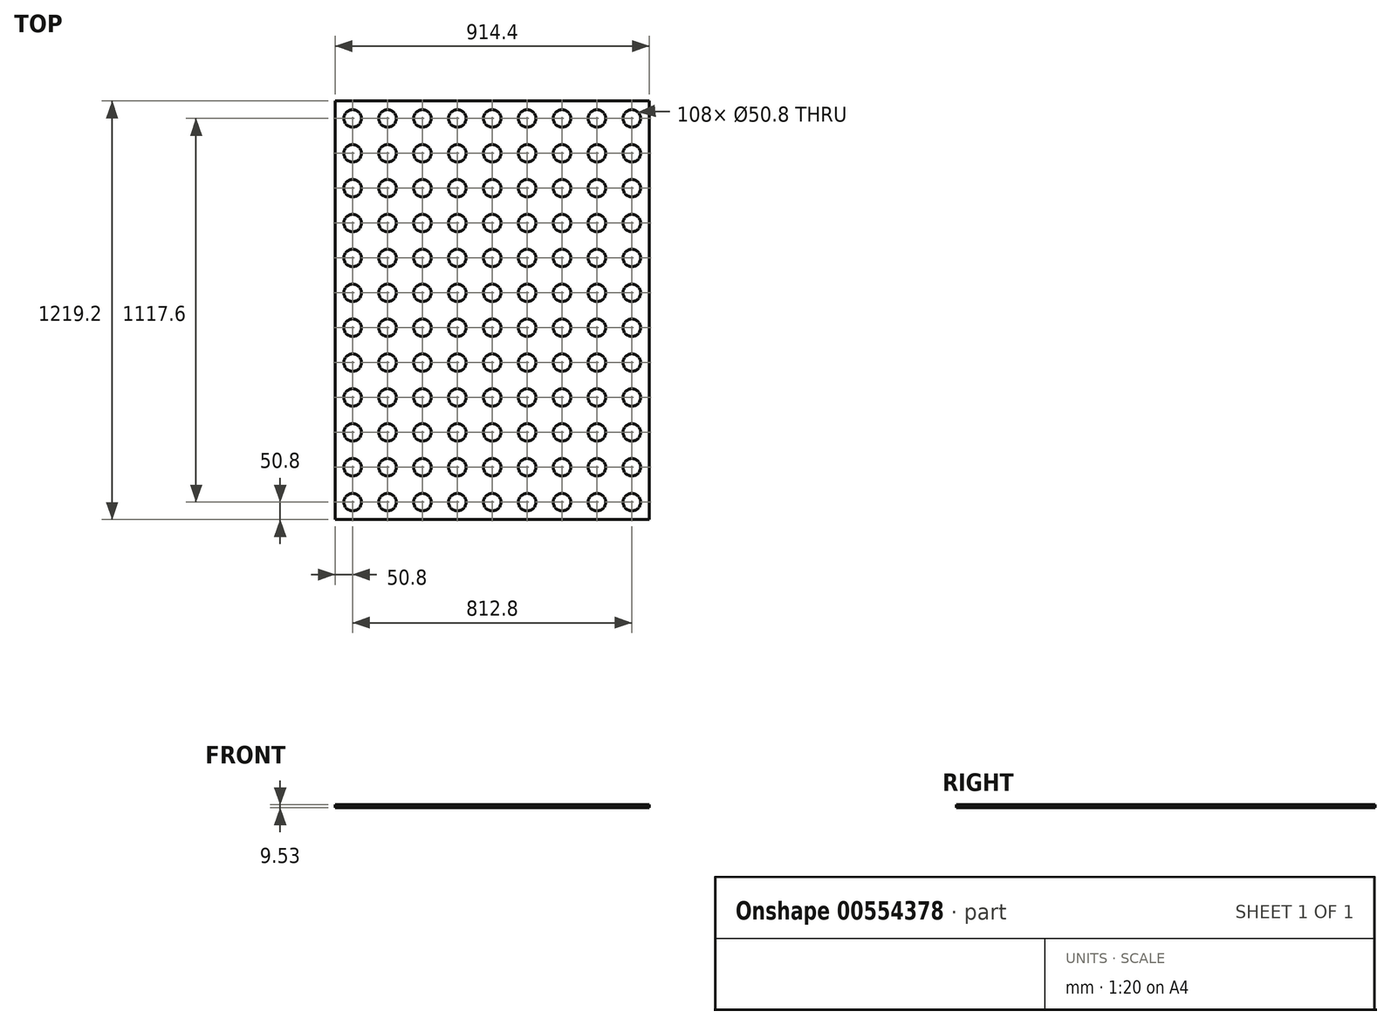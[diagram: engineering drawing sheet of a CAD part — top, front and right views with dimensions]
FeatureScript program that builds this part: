
annotation { "Feature Type Name" : "Feature", "Feature Type Description" : "" }
export const myFeature = defineFeature(function(context is Context, id is Id, definition is map)
    precondition{}
    {
        {
            var Q0;
            Q0=qCreatedBy(makeId("Top.planeOp"),FACE);
            var sketch = newSketch(context, id + "F0", { "sketchPlane" : qUnion([Q0])});
            skLineSegment(sketch, "E0.bottom", {"start": v(457.2, 609.6) * mm, "end": v(-457.2, 609.6) * mm});
            skLineSegment(sketch, "E0.top", {"start": v(457.2, -609.6) * mm, "end": v(-457.2, -609.6) * mm});
            skLineSegment(sketch, "E0.left", {"start": v(457.2, 609.6) * mm, "end": v(457.2, -609.6) * mm});
            skLineSegment(sketch, "E0.right", {"start": v(-457.2, 609.6) * mm, "end": v(-457.2, -609.6) * mm});
            skPoint(sketch, "E0.middle", {"position": v(0, 0) * mm});
            skSolve(sketch);
        }
        {
            var Q0;
            Q0 = qSketchRegion(id + "F0", true);
            extrude(context, id + "F1", {"entities" : qUnion([Q0]), "depth" : 9.52 * mm, "offsetDistance" : 25.4 * mm});
        }
        {
            var Q0;
            Q0=makeQuery(id+"F1.opExtrude","CAP_FACE",FACE,{"disambiguationData":[OSD([sQuery(id+"F0.wireOp",EDGE,"E0.bottom"),sQuery(id+"F0.wireOp",EDGE,"E0.top"),sQuery(id+"F0.wireOp",EDGE,"E0.left"),sQuery(id+"F0.wireOp",EDGE,"E0.right")])],"isStart":false});
            var sketch = newSketch(context, id + "F2", { "sketchPlane" : qUnion([Q0])});
            skCircle(sketch, "E1", {"center": v(-406.4, 558.8) * mm, "radius": 25.4 * mm});
            skCircle(sketch, "E2.1.0.0", {"center": v(-304.8, 558.8) * mm, "radius": 25.4 * mm});
            skCircle(sketch, "E2.2.0.0", {"center": v(-203.2, 558.8) * mm, "radius": 25.4 * mm});
            skCircle(sketch, "E2.3.0.0", {"center": v(-101.6, 558.8) * mm, "radius": 25.4 * mm});
            skCircle(sketch, "E2.4.0.0", {"center": v(0, 558.8) * mm, "radius": 25.4 * mm});
            skCircle(sketch, "E2.5.0.0", {"center": v(101.6, 558.8) * mm, "radius": 25.4 * mm});
            skCircle(sketch, "E2.6.0.0", {"center": v(203.2, 558.8) * mm, "radius": 25.4 * mm});
            skCircle(sketch, "E2.7.0.0", {"center": v(304.8, 558.8) * mm, "radius": 25.4 * mm});
            skCircle(sketch, "E2.8.0.0", {"center": v(406.4, 558.8) * mm, "radius": 25.4 * mm});
            skLineSegment(sketch, "E2.direction1", {"start": v(-406.4, 558.8) * mm, "end": v(-304.8, 558.8) * mm, "construction": true});
            skCircle(sketch, "E3.0.1.0", {"center": v(-101.6, 457.2) * mm, "radius": 25.4 * mm});
            skCircle(sketch, "E3.0.1.1", {"center": v(0, 457.2) * mm, "radius": 25.4 * mm});
            skCircle(sketch, "E3.0.1.2", {"center": v(101.6, 457.2) * mm, "radius": 25.4 * mm});
            skCircle(sketch, "E3.0.1.3", {"center": v(203.2, 457.2) * mm, "radius": 25.4 * mm});
            skLineSegment(sketch, "E3.0.1.4", {"start": v(-406.4, 457.2) * mm, "end": v(-304.8, 457.2) * mm, "construction": true});
            skCircle(sketch, "E3.0.1.5", {"center": v(406.4, 457.2) * mm, "radius": 25.4 * mm});
            skCircle(sketch, "E3.0.1.6", {"center": v(-203.2, 457.2) * mm, "radius": 25.4 * mm});
            skCircle(sketch, "E3.0.1.7", {"center": v(-304.8, 457.2) * mm, "radius": 25.4 * mm});
            skCircle(sketch, "E3.0.1.8", {"center": v(-406.4, 457.2) * mm, "radius": 25.4 * mm});
            skCircle(sketch, "E3.0.1.9", {"center": v(304.8, 457.2) * mm, "radius": 25.4 * mm});
            skCircle(sketch, "E3.0.2.0", {"center": v(-101.6, 355.6) * mm, "radius": 25.4 * mm});
            skCircle(sketch, "E3.0.2.1", {"center": v(0, 355.6) * mm, "radius": 25.4 * mm});
            skCircle(sketch, "E3.0.2.2", {"center": v(101.6, 355.6) * mm, "radius": 25.4 * mm});
            skCircle(sketch, "E3.0.2.3", {"center": v(203.2, 355.6) * mm, "radius": 25.4 * mm});
            skLineSegment(sketch, "E3.0.2.4", {"start": v(-406.4, 355.6) * mm, "end": v(-304.8, 355.6) * mm, "construction": true});
            skCircle(sketch, "E3.0.2.5", {"center": v(406.4, 355.6) * mm, "radius": 25.4 * mm});
            skCircle(sketch, "E3.0.2.6", {"center": v(-203.2, 355.6) * mm, "radius": 25.4 * mm});
            skCircle(sketch, "E3.0.2.7", {"center": v(-304.8, 355.6) * mm, "radius": 25.4 * mm});
            skCircle(sketch, "E3.0.2.8", {"center": v(-406.4, 355.6) * mm, "radius": 25.4 * mm});
            skCircle(sketch, "E3.0.2.9", {"center": v(304.8, 355.6) * mm, "radius": 25.4 * mm});
            skCircle(sketch, "E3.0.3.0", {"center": v(-101.6, 254) * mm, "radius": 25.4 * mm});
            skCircle(sketch, "E3.0.3.1", {"center": v(0, 254) * mm, "radius": 25.4 * mm});
            skCircle(sketch, "E3.0.3.2", {"center": v(101.6, 254) * mm, "radius": 25.4 * mm});
            skCircle(sketch, "E3.0.3.3", {"center": v(203.2, 254) * mm, "radius": 25.4 * mm});
            skLineSegment(sketch, "E3.0.3.4", {"start": v(-406.4, 254) * mm, "end": v(-304.8, 254) * mm, "construction": true});
            skCircle(sketch, "E3.0.3.5", {"center": v(406.4, 254) * mm, "radius": 25.4 * mm});
            skCircle(sketch, "E3.0.3.6", {"center": v(-203.2, 254) * mm, "radius": 25.4 * mm});
            skCircle(sketch, "E3.0.3.7", {"center": v(-304.8, 254) * mm, "radius": 25.4 * mm});
            skCircle(sketch, "E3.0.3.8", {"center": v(-406.4, 254) * mm, "radius": 25.4 * mm});
            skCircle(sketch, "E3.0.3.9", {"center": v(304.8, 254) * mm, "radius": 25.4 * mm});
            skCircle(sketch, "E3.0.4.0", {"center": v(-101.6, 152.4) * mm, "radius": 25.4 * mm});
            skCircle(sketch, "E3.0.4.1", {"center": v(0, 152.4) * mm, "radius": 25.4 * mm});
            skCircle(sketch, "E3.0.4.2", {"center": v(101.6, 152.4) * mm, "radius": 25.4 * mm});
            skCircle(sketch, "E3.0.4.3", {"center": v(203.2, 152.4) * mm, "radius": 25.4 * mm});
            skLineSegment(sketch, "E3.0.4.4", {"start": v(-406.4, 152.4) * mm, "end": v(-304.8, 152.4) * mm, "construction": true});
            skCircle(sketch, "E3.0.4.5", {"center": v(406.4, 152.4) * mm, "radius": 25.4 * mm});
            skCircle(sketch, "E3.0.4.6", {"center": v(-203.2, 152.4) * mm, "radius": 25.4 * mm});
            skCircle(sketch, "E3.0.4.7", {"center": v(-304.8, 152.4) * mm, "radius": 25.4 * mm});
            skCircle(sketch, "E3.0.4.8", {"center": v(-406.4, 152.4) * mm, "radius": 25.4 * mm});
            skCircle(sketch, "E3.0.4.9", {"center": v(304.8, 152.4) * mm, "radius": 25.4 * mm});
            skCircle(sketch, "E3.0.5.0", {"center": v(-101.6, 50.8) * mm, "radius": 25.4 * mm});
            skCircle(sketch, "E3.0.5.1", {"center": v(0, 50.8) * mm, "radius": 25.4 * mm});
            skCircle(sketch, "E3.0.5.2", {"center": v(101.6, 50.8) * mm, "radius": 25.4 * mm});
            skCircle(sketch, "E3.0.5.3", {"center": v(203.2, 50.8) * mm, "radius": 25.4 * mm});
            skLineSegment(sketch, "E3.0.5.4", {"start": v(-406.4, 50.8) * mm, "end": v(-304.8, 50.8) * mm, "construction": true});
            skCircle(sketch, "E3.0.5.5", {"center": v(406.4, 50.8) * mm, "radius": 25.4 * mm});
            skCircle(sketch, "E3.0.5.6", {"center": v(-203.2, 50.8) * mm, "radius": 25.4 * mm});
            skCircle(sketch, "E3.0.5.7", {"center": v(-304.8, 50.8) * mm, "radius": 25.4 * mm});
            skCircle(sketch, "E3.0.5.8", {"center": v(-406.4, 50.8) * mm, "radius": 25.4 * mm});
            skCircle(sketch, "E3.0.5.9", {"center": v(304.8, 50.8) * mm, "radius": 25.4 * mm});
            skCircle(sketch, "E3.0.6.0", {"center": v(-101.6, -50.8) * mm, "radius": 25.4 * mm});
            skCircle(sketch, "E3.0.6.1", {"center": v(0, -50.8) * mm, "radius": 25.4 * mm});
            skCircle(sketch, "E3.0.6.2", {"center": v(101.6, -50.8) * mm, "radius": 25.4 * mm});
            skCircle(sketch, "E3.0.6.3", {"center": v(203.2, -50.8) * mm, "radius": 25.4 * mm});
            skLineSegment(sketch, "E3.0.6.4", {"start": v(-406.4, -50.8) * mm, "end": v(-304.8, -50.8) * mm, "construction": true});
            skCircle(sketch, "E3.0.6.5", {"center": v(406.4, -50.8) * mm, "radius": 25.4 * mm});
            skCircle(sketch, "E3.0.6.6", {"center": v(-203.2, -50.8) * mm, "radius": 25.4 * mm});
            skCircle(sketch, "E3.0.6.7", {"center": v(-304.8, -50.8) * mm, "radius": 25.4 * mm});
            skCircle(sketch, "E3.0.6.8", {"center": v(-406.4, -50.8) * mm, "radius": 25.4 * mm});
            skCircle(sketch, "E3.0.6.9", {"center": v(304.8, -50.8) * mm, "radius": 25.4 * mm});
            skCircle(sketch, "E3.0.7.0", {"center": v(-101.6, -152.4) * mm, "radius": 25.4 * mm});
            skCircle(sketch, "E3.0.7.1", {"center": v(0, -152.4) * mm, "radius": 25.4 * mm});
            skCircle(sketch, "E3.0.7.2", {"center": v(101.6, -152.4) * mm, "radius": 25.4 * mm});
            skCircle(sketch, "E3.0.7.3", {"center": v(203.2, -152.4) * mm, "radius": 25.4 * mm});
            skLineSegment(sketch, "E3.0.7.4", {"start": v(-406.4, -152.4) * mm, "end": v(-304.8, -152.4) * mm, "construction": true});
            skCircle(sketch, "E3.0.7.5", {"center": v(406.4, -152.4) * mm, "radius": 25.4 * mm});
            skCircle(sketch, "E3.0.7.6", {"center": v(-203.2, -152.4) * mm, "radius": 25.4 * mm});
            skCircle(sketch, "E3.0.7.7", {"center": v(-304.8, -152.4) * mm, "radius": 25.4 * mm});
            skCircle(sketch, "E3.0.7.8", {"center": v(-406.4, -152.4) * mm, "radius": 25.4 * mm});
            skCircle(sketch, "E3.0.7.9", {"center": v(304.8, -152.4) * mm, "radius": 25.4 * mm});
            skCircle(sketch, "E3.0.8.0", {"center": v(-101.6, -254) * mm, "radius": 25.4 * mm});
            skCircle(sketch, "E3.0.8.1", {"center": v(0, -254) * mm, "radius": 25.4 * mm});
            skCircle(sketch, "E3.0.8.2", {"center": v(101.6, -254) * mm, "radius": 25.4 * mm});
            skCircle(sketch, "E3.0.8.3", {"center": v(203.2, -254) * mm, "radius": 25.4 * mm});
            skLineSegment(sketch, "E3.0.8.4", {"start": v(-406.4, -254) * mm, "end": v(-304.8, -254) * mm, "construction": true});
            skCircle(sketch, "E3.0.8.5", {"center": v(406.4, -254) * mm, "radius": 25.4 * mm});
            skCircle(sketch, "E3.0.8.6", {"center": v(-203.2, -254) * mm, "radius": 25.4 * mm});
            skCircle(sketch, "E3.0.8.7", {"center": v(-304.8, -254) * mm, "radius": 25.4 * mm});
            skCircle(sketch, "E3.0.8.8", {"center": v(-406.4, -254) * mm, "radius": 25.4 * mm});
            skCircle(sketch, "E3.0.8.9", {"center": v(304.8, -254) * mm, "radius": 25.4 * mm});
            skCircle(sketch, "E3.0.9.0", {"center": v(-101.6, -355.6) * mm, "radius": 25.4 * mm});
            skCircle(sketch, "E3.0.9.1", {"center": v(0, -355.6) * mm, "radius": 25.4 * mm});
            skCircle(sketch, "E3.0.9.2", {"center": v(101.6, -355.6) * mm, "radius": 25.4 * mm});
            skCircle(sketch, "E3.0.9.3", {"center": v(203.2, -355.6) * mm, "radius": 25.4 * mm});
            skLineSegment(sketch, "E3.0.9.4", {"start": v(-406.4, -355.6) * mm, "end": v(-304.8, -355.6) * mm, "construction": true});
            skCircle(sketch, "E3.0.9.5", {"center": v(406.4, -355.6) * mm, "radius": 25.4 * mm});
            skCircle(sketch, "E3.0.9.6", {"center": v(-203.2, -355.6) * mm, "radius": 25.4 * mm});
            skCircle(sketch, "E3.0.9.7", {"center": v(-304.8, -355.6) * mm, "radius": 25.4 * mm});
            skCircle(sketch, "E3.0.9.8", {"center": v(-406.4, -355.6) * mm, "radius": 25.4 * mm});
            skCircle(sketch, "E3.0.9.9", {"center": v(304.8, -355.6) * mm, "radius": 25.4 * mm});
            skCircle(sketch, "E3.0.10.0", {"center": v(-101.6, -457.2) * mm, "radius": 25.4 * mm});
            skCircle(sketch, "E3.0.10.1", {"center": v(0, -457.2) * mm, "radius": 25.4 * mm});
            skCircle(sketch, "E3.0.10.2", {"center": v(101.6, -457.2) * mm, "radius": 25.4 * mm});
            skCircle(sketch, "E3.0.10.3", {"center": v(203.2, -457.2) * mm, "radius": 25.4 * mm});
            skLineSegment(sketch, "E3.0.10.4", {"start": v(-406.4, -457.2) * mm, "end": v(-304.8, -457.2) * mm, "construction": true});
            skCircle(sketch, "E3.0.10.5", {"center": v(406.4, -457.2) * mm, "radius": 25.4 * mm});
            skCircle(sketch, "E3.0.10.6", {"center": v(-203.2, -457.2) * mm, "radius": 25.4 * mm});
            skCircle(sketch, "E3.0.10.7", {"center": v(-304.8, -457.2) * mm, "radius": 25.4 * mm});
            skCircle(sketch, "E3.0.10.8", {"center": v(-406.4, -457.2) * mm, "radius": 25.4 * mm});
            skCircle(sketch, "E3.0.10.9", {"center": v(304.8, -457.2) * mm, "radius": 25.4 * mm});
            skCircle(sketch, "E3.0.11.0", {"center": v(-101.6, -558.8) * mm, "radius": 25.4 * mm});
            skCircle(sketch, "E3.0.11.1", {"center": v(0, -558.8) * mm, "radius": 25.4 * mm});
            skCircle(sketch, "E3.0.11.2", {"center": v(101.6, -558.8) * mm, "radius": 25.4 * mm});
            skCircle(sketch, "E3.0.11.3", {"center": v(203.2, -558.8) * mm, "radius": 25.4 * mm});
            skLineSegment(sketch, "E3.0.11.4", {"start": v(-406.4, -558.8) * mm, "end": v(-304.8, -558.8) * mm, "construction": true});
            skCircle(sketch, "E3.0.11.5", {"center": v(406.4, -558.8) * mm, "radius": 25.4 * mm});
            skCircle(sketch, "E3.0.11.6", {"center": v(-203.2, -558.8) * mm, "radius": 25.4 * mm});
            skCircle(sketch, "E3.0.11.7", {"center": v(-304.8, -558.8) * mm, "radius": 25.4 * mm});
            skCircle(sketch, "E3.0.11.8", {"center": v(-406.4, -558.8) * mm, "radius": 25.4 * mm});
            skCircle(sketch, "E3.0.11.9", {"center": v(304.8, -558.8) * mm, "radius": 25.4 * mm});
            skLineSegment(sketch, "E3.direction1", {"start": v(-406.4, 558.8) * mm, "end": v(-381, 558.8) * mm, "construction": true});
            skLineSegment(sketch, "E3.direction2", {"start": v(-406.4, 558.8) * mm, "end": v(-406.4, 457.2) * mm, "construction": true});
            skSolve(sketch);
        }
        {
            var Q0;
            Q0 = qSketchRegion(id + "F2", true);
            extrude(context, id + "F3", {"entities" : qUnion([Q0]), "operationType" : NewBodyOperationType.REMOVE, "endBound" : BoundingType.UP_TO_NEXT, "oppositeDirection" : true, "depth" : 25.4 * mm, "offsetDistance" : 25.4 * mm});
        }
    });
